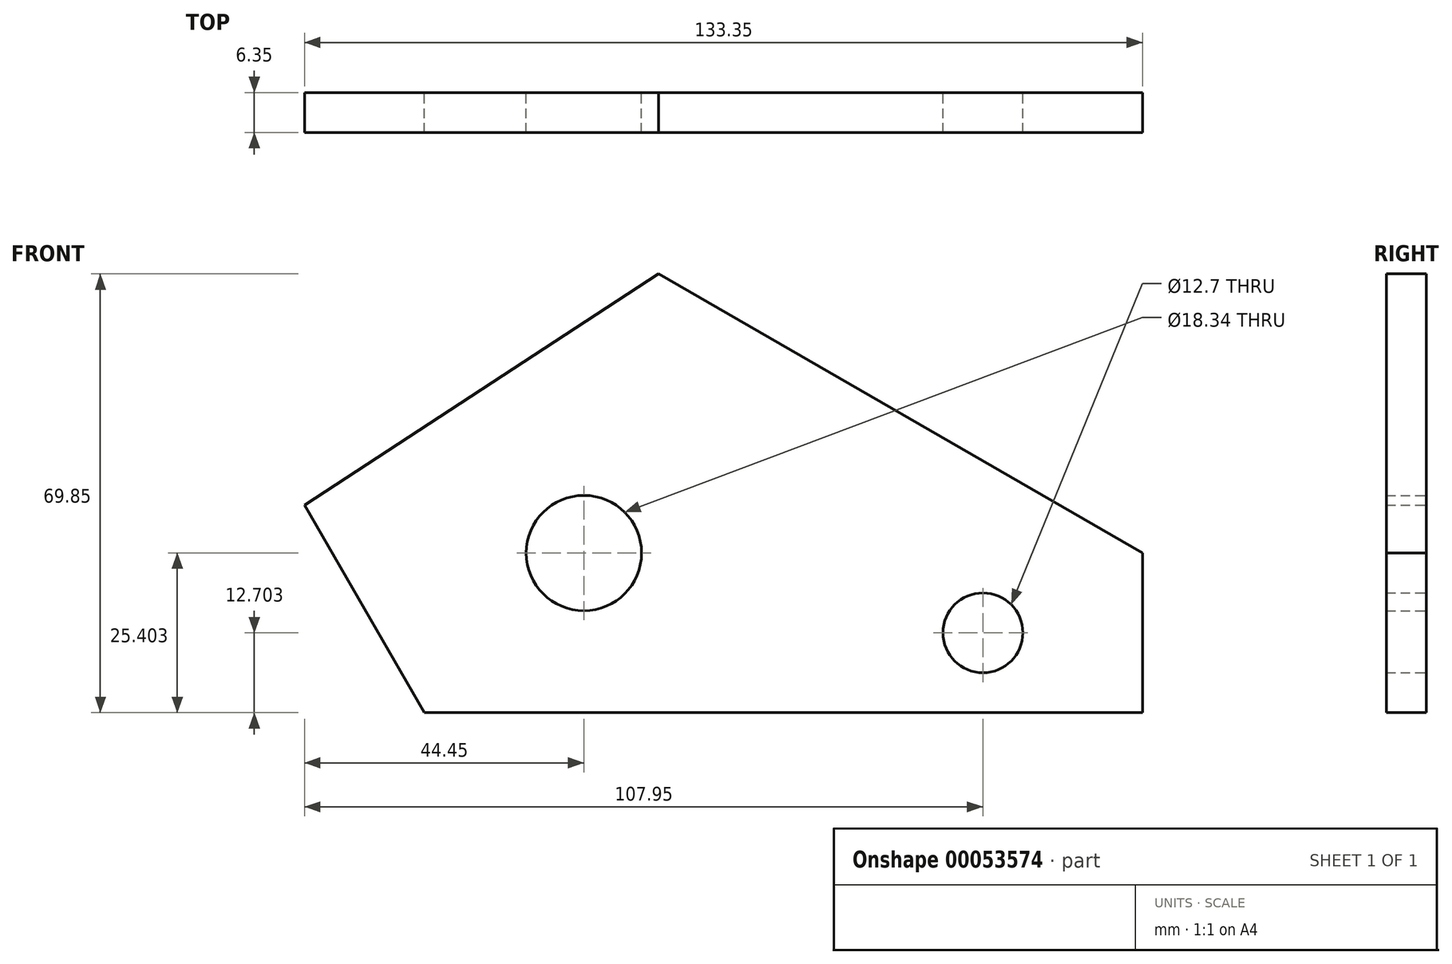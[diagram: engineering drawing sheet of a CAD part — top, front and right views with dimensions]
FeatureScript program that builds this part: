
annotation { "Feature Type Name" : "Feature", "Feature Type Description" : "" }
export const myFeature = defineFeature(function(context is Context, id is Id, definition is map)
    precondition{}
    {
        {
            var Q0;
            Q0=qCreatedBy(makeId("Front.planeOp"),FACE);
            var sketch = newSketch(context, id + "F0", { "sketchPlane" : qUnion([Q0])});
            skLineSegment(sketch, "E0", {"start": v(-88.9, -2.53) * mm, "end": v(25.4, -2.53) * mm});
            skLineSegment(sketch, "E1", {"start": v(-88.9, -2.53) * mm, "end": v(-107.95, 30.47) * mm});
            skLineSegment(sketch, "E2", {"start": v(25.4, -2.53) * mm, "end": v(25.4, 22.87) * mm});
            skLineSegment(sketch, "E3", {"start": v(25.4, 22.87) * mm, "end": v(-51.59, 67.32) * mm});
            skLineSegment(sketch, "E4", {"start": v(-107.95, 30.47) * mm, "end": v(-51.59, 67.32) * mm});
            skPoint(sketch, "E5", {"position": v(0, -2.53) * mm});
            skPoint(sketch, "E6", {"position": v(25.4, 10.17) * mm});
            skCircle(sketch, "E7", {"center": v(0, 10.17) * mm, "radius": 6.35 * mm});
            skPoint(sketch, "E8", {"position": v(-63.5, -2.53) * mm});
            skCircle(sketch, "E9", {"center": v(-63.5, 22.87) * mm, "radius": 9.17 * mm});
            skSolve(sketch);
        }
        {
            var Q0;
            Q0 = qSketchRegion(id + "F0", true);
            var Q1;
            Q1=makeQuery(id+"F0.imprint","IMPRINT",FACE,{"disambiguationData":[TD([[makeQuery(id+"F0.imprint","IMPRINT",EDGE,{"derivedFrom":sQuery(id+"F0.wireOp",EDGE,"E0")}),1.0]])]});
            extrude(context, id + "F1", {"entities" : qUnion([Q0, Q1]), "depth" : 6.35 * mm});
        }
    });
